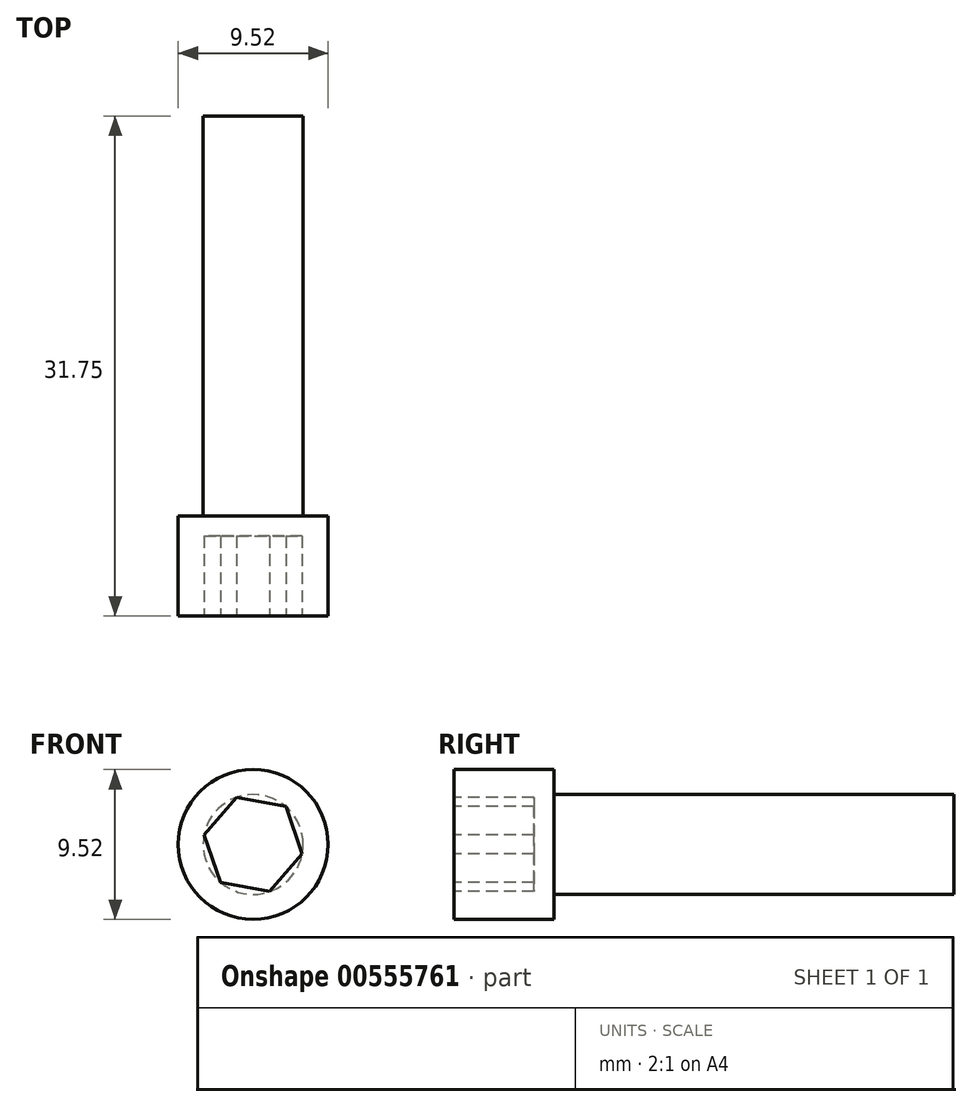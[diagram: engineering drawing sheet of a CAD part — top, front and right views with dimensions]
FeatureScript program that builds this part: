
annotation { "Feature Type Name" : "Feature", "Feature Type Description" : "" }
export const myFeature = defineFeature(function(context is Context, id is Id, definition is map)
    precondition{}
    {
        {
            var Q0;
            Q0=qCreatedBy(makeId("Front.planeOp"),FACE);
            var sketch = newSketch(context, id + "F0", { "sketchPlane" : qUnion([Q0])});
            skCircle(sketch, "E0", {"center": v(0, 0) * mm, "radius": 3.18 * mm});
            skSolve(sketch);
        }
        {
            var Q0;
            Q0 = qSketchRegion(id + "F0", true);
            extrude(context, id + "F1", {"entities" : qUnion([Q0]), "depth" : 25.4 * mm, "offsetDistance" : 25.4 * mm});
        }
        {
            var Q0;
            Q0=makeQuery(id+"F1.opExtrude","CAP_FACE",FACE,{"disambiguationData":[OSD([sQuery(id+"F0.wireOp",EDGE,"E0")])],"isStart":false});
            var sketch = newSketch(context, id + "F2", { "sketchPlane" : qUnion([Q0])});
            skCircle(sketch, "E1", {"center": v(0, 0) * mm, "radius": 4.76 * mm});
            skSolve(sketch);
        }
        {
            var Q0;
            Q0 = qSketchRegion(id + "F2", true);
            extrude(context, id + "F3", {"entities" : qUnion([Q0]), "operationType" : NewBodyOperationType.ADD, "depth" : 6.35 * mm, "offsetDistance" : 25.4 * mm});
        }
        {
            var Q0;
            Q0=makeQuery(id+"F3.opExtrude","CAP_FACE",FACE,{"disambiguationData":[OSD([sQuery(id+"F2.wireOp",EDGE,"E1")])],"isStart":false});
            var sketch = newSketch(context, id + "F4", { "sketchPlane" : qUnion([Q0])});
            skCircle(sketch, "E2.cCircle", {"center": v(0, 0) * mm, "radius": 3.18 * mm, "construction": true});
            skLineSegment(sketch, "E2.0", {"start": v(-2.07, -2.4) * mm, "end": v(-3.12, 0.6) * mm});
            skLineSegment(sketch, "E2.1", {"start": v(-3.12, 0.6) * mm, "end": v(-1.05, 3) * mm});
            skLineSegment(sketch, "E2.2", {"start": v(-1.05, 3) * mm, "end": v(2.07, 2.4) * mm});
            skLineSegment(sketch, "E2.3", {"start": v(2.07, 2.4) * mm, "end": v(3.12, -0.6) * mm});
            skLineSegment(sketch, "E2.4", {"start": v(3.12, -0.6) * mm, "end": v(1.05, -3) * mm});
            skLineSegment(sketch, "E2.5", {"start": v(1.05, -3) * mm, "end": v(-2.07, -2.4) * mm});
            skSolve(sketch);
        }
        {
            var Q0;
            Q0=makeQuery(id+"F4.imprint","IMPRINT",FACE,{"disambiguationData":[TD([[makeQuery(id+"F4.imprint","IMPRINT",EDGE,{"derivedFrom":sQuery(id+"F4.wireOp",EDGE,"E2.0")}),-1.0]])]});
            extrude(context, id + "F5", {"entities" : qUnion([Q0]), "operationType" : NewBodyOperationType.REMOVE, "oppositeDirection" : true, "depth" : 5.08 * mm, "offsetDistance" : 25.4 * mm});
        }
    });
